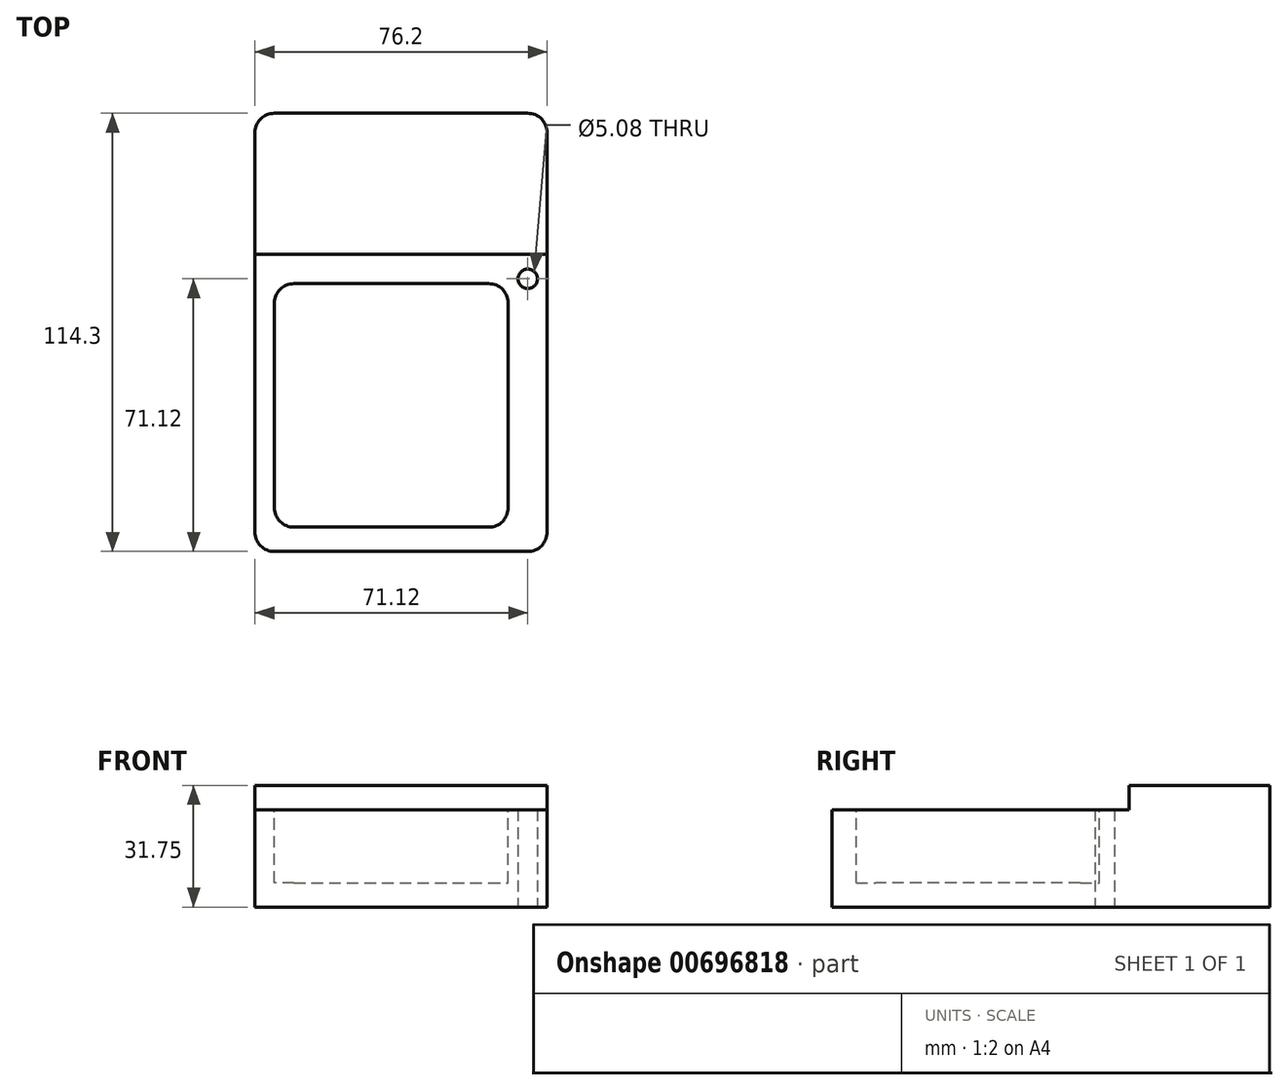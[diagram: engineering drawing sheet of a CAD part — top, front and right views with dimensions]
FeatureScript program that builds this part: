
annotation { "Feature Type Name" : "Feature", "Feature Type Description" : "" }
export const myFeature = defineFeature(function(context is Context, id is Id, definition is map)
    precondition{}
    {
        {
            var Q0;
            Q0=qCreatedBy(makeId("Top.planeOp"),FACE);
            var sketch = newSketch(context, id + "F0", { "sketchPlane" : qUnion([Q0])});
            skLineSegment(sketch, "E0.bottom", {"start": v(38.1, -57.15) * mm, "end": v(-38.1, -57.15) * mm});
            skLineSegment(sketch, "E0.top", {"start": v(38.1, 57.15) * mm, "end": v(-38.1, 57.15) * mm});
            skLineSegment(sketch, "E0.left", {"start": v(38.1, -57.15) * mm, "end": v(38.1, 57.15) * mm});
            skLineSegment(sketch, "E0.right", {"start": v(-38.1, -57.15) * mm, "end": v(-38.1, 57.15) * mm});
            skPoint(sketch, "E0.middle", {"position": v(0, 0) * mm});
            skCircle(sketch, "E1", {"center": v(33.02, 13.97) * mm, "radius": 2.54 * mm});
            skSolve(sketch);
        }
        {
            var Q0;
            Q0=qSketchRegion(id+"F0",true);
            extrude(context, id + "F1", {"entities" : qUnion([Q0]), "endBound" : BoundingType.SYMMETRIC, "depth" : 25.4 * mm, "offsetDistance" : 25.4 * mm});
        }
        {
            var Q0;
            Q0=makeQuery(id+"F1.opExtrude","SWEPT_EDGE",EDGE,{"disambiguationData":[OSD([sQuery(id+"F0.wireOp",EDGE,"E0.bottom"),sQuery(id+"F0.wireOp",EDGE,"E0.right")])]});
            var Q1;
            Q1=makeQuery(id+"F1.opExtrude","SWEPT_EDGE",EDGE,{"disambiguationData":[OSD([sQuery(id+"F0.wireOp",EDGE,"E0.bottom"),sQuery(id+"F0.wireOp",EDGE,"E0.left")])]});
            var Q2;
            Q2=makeQuery(id+"F1.opExtrude","SWEPT_EDGE",EDGE,{"disambiguationData":[OSD([sQuery(id+"F0.wireOp",EDGE,"E0.top"),sQuery(id+"F0.wireOp",EDGE,"E0.right")])]});
            var Q3;
            Q3=makeQuery(id+"F1.opExtrude","SWEPT_EDGE",EDGE,{"disambiguationData":[OSD([sQuery(id+"F0.wireOp",EDGE,"E0.top"),sQuery(id+"F0.wireOp",EDGE,"E0.left")])]});
            fillet(context, id + "F2", {"entities" : qUnion([Q0, Q1, Q2, Q3]), "radius" : 5.08 * mm, "tangentPropagation" : true, "allowEdgeOverflow" : false});
        }
        {
            var Q0;
            Q0=makeQuery(id+"F1.opExtrude","CAP_FACE",FACE,{"disambiguationData":[OSD([sQuery(id+"F0.wireOp",EDGE,"E0.bottom"),sQuery(id+"F0.wireOp",EDGE,"E0.top"),sQuery(id+"F0.wireOp",EDGE,"E0.left"),sQuery(id+"F0.wireOp",EDGE,"E0.right"),sQuery(id+"F0.wireOp",EDGE,"E1"),sQuery(id+"F0.wireOp",EDGE,"BQglXwos-gW2q-lWl8-8KG2-oqi90ELSd8i5")])],"isStart":false});
            var sketch = newSketch(context, id + "F3", { "sketchPlane" : qUnion([Q0])});
            skPoint(sketch, "E2.oppositeSnap0", {"position": v(36.61, 55.66) * mm});
            skLineSegment(sketch, "E3.bottom", {"start": v(-38.1, 57.15) * mm, "end": v(38.1, 57.15) * mm});
            skLineSegment(sketch, "E3.top", {"start": v(-38.1, 20.32) * mm, "end": v(38.1, 20.32) * mm});
            skLineSegment(sketch, "E3.left", {"start": v(-38.1, 57.15) * mm, "end": v(-38.1, 20.32) * mm});
            skLineSegment(sketch, "E3.right", {"start": v(38.1, 57.15) * mm, "end": v(38.1, 20.32) * mm});
            skSolve(sketch);
        }
        {
            var Q0;
            Q0=makeQuery(id+"F3.imprint","IMPRINT",FACE,{"disambiguationData":[TD([[makeQuery(id+"F3.imprint","IMPRINT",EDGE,{"derivedFrom":sQuery(id+"F3.wireOp",EDGE,"E3.bottom")}),1.0]])]});
            extrude(context, id + "F4", {"entities" : qUnion([Q0]), "operationType" : NewBodyOperationType.ADD, "depth" : 6.35 * mm, "offsetDistance" : 25.4 * mm});
        }
        {
            var Q0;
            Q0=makeQuery(id+"F1.opExtrude","CAP_FACE",FACE,{"disambiguationData":[OSD([sQuery(id+"F0.wireOp",EDGE,"E0.bottom"),sQuery(id+"F0.wireOp",EDGE,"E0.top"),sQuery(id+"F0.wireOp",EDGE,"E0.left"),sQuery(id+"F0.wireOp",EDGE,"E0.right"),sQuery(id+"F0.wireOp",EDGE,"E1"),sQuery(id+"F0.wireOp",EDGE,"BQglXwos-gW2q-lWl8-8KG2-oqi90ELSd8i5")])],"isStart":false});
            var sketch = newSketch(context, id + "F5", { "sketchPlane" : qUnion([Q0])});
            skLineSegment(sketch, "E4.bottom", {"start": v(-33.02, 12.7) * mm, "end": v(27.94, 12.7) * mm});
            skLineSegment(sketch, "E4.top", {"start": v(-33.02, -50.8) * mm, "end": v(27.94, -50.8) * mm});
            skLineSegment(sketch, "E4.left", {"start": v(-33.02, 12.7) * mm, "end": v(-33.02, -50.8) * mm});
            skLineSegment(sketch, "E4.right", {"start": v(27.94, 12.7) * mm, "end": v(27.94, -50.8) * mm});
            skSolve(sketch);
        }
        {
            var Q0;
            Q0=qSketchRegion(id+"F5",true);
            extrude(context, id + "F6", {"entities" : qUnion([Q0]), "operationType" : NewBodyOperationType.REMOVE, "oppositeDirection" : true, "depth" : 19.05 * mm, "offsetDistance" : 25.4 * mm});
        }
        {
            var Q0;
            Q0=makeQuery(id+"F6.boolean.opBoolean","COPY",EDGE,{"derivedFrom":makeQuery(id+"F6.opExtrude","SWEPT_EDGE",EDGE,{"disambiguationData":[OSD([sQuery(id+"F5.wireOp",EDGE,"E4.bottom"),sQuery(id+"F5.wireOp",EDGE,"E4.left")])]})});
            var Q1;
            Q1=makeQuery(id+"F6.boolean.opBoolean","COPY",EDGE,{"derivedFrom":makeQuery(id+"F6.opExtrude","SWEPT_EDGE",EDGE,{"disambiguationData":[OSD([sQuery(id+"F5.wireOp",EDGE,"E4.top"),sQuery(id+"F5.wireOp",EDGE,"E4.left")])]})});
            var Q2;
            Q2=makeQuery(id+"F6.boolean.opBoolean","COPY",EDGE,{"derivedFrom":makeQuery(id+"F6.opExtrude","SWEPT_EDGE",EDGE,{"disambiguationData":[OSD([sQuery(id+"F5.wireOp",EDGE,"E4.bottom"),sQuery(id+"F5.wireOp",EDGE,"E4.right")])]})});
            var Q3;
            Q3=makeQuery(id+"F6.boolean.opBoolean","COPY",EDGE,{"derivedFrom":makeQuery(id+"F6.opExtrude","SWEPT_EDGE",EDGE,{"disambiguationData":[OSD([sQuery(id+"F5.wireOp",EDGE,"E4.top"),sQuery(id+"F5.wireOp",EDGE,"E4.right")])]})});
            fillet(context, id + "F7", {"entities" : qUnion([Q0, Q1, Q2, Q3]), "radius" : 5.08 * mm, "tangentPropagation" : true, "allowEdgeOverflow" : false});
        }
    });
